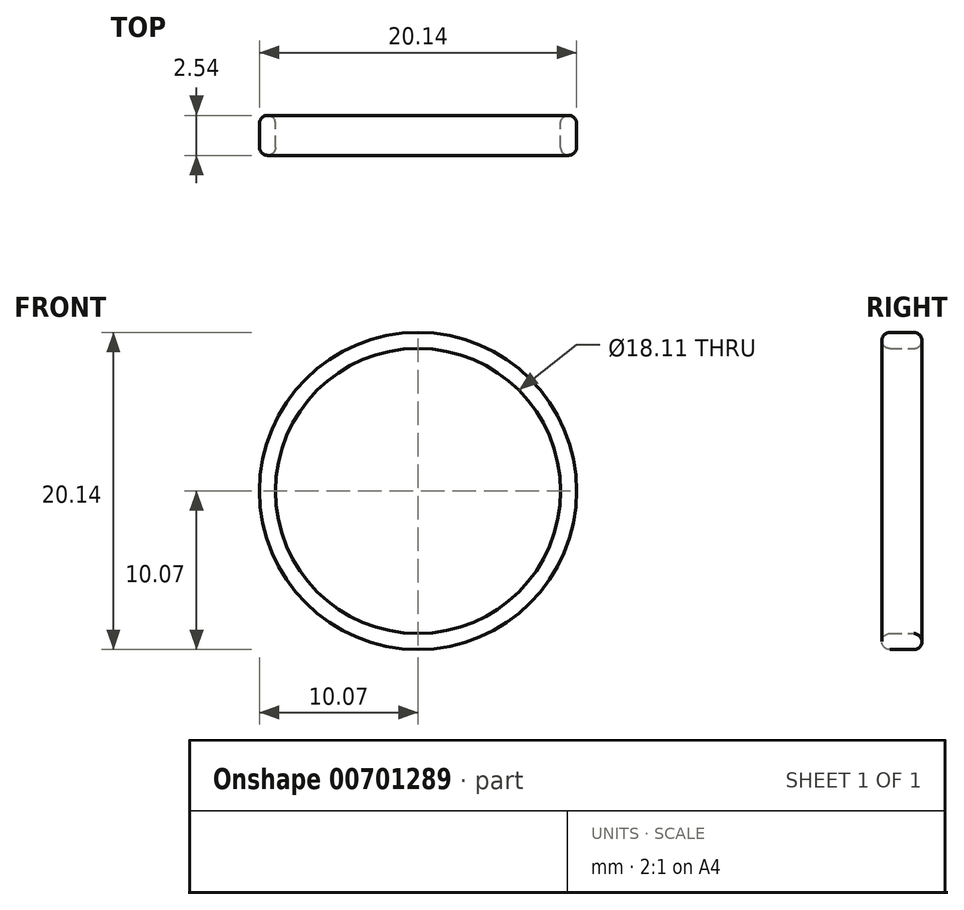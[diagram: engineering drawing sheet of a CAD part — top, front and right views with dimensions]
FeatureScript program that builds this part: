
annotation { "Feature Type Name" : "Feature", "Feature Type Description" : "" }
export const myFeature = defineFeature(function(context is Context, id is Id, definition is map)
    precondition{}
    {
        {
            var Q0;
            Q0=qCreatedBy(makeId("Front.planeOp"),FACE);
            var sketch = newSketch(context, id + "F0", { "sketchPlane" : qUnion([Q0])});
            skCircle(sketch, "E0", {"center": v(0, 0) * mm, "radius": 9.06 * mm});
            skCircle(sketch, "E1", {"center": v(0, 0) * mm, "radius": 10.07 * mm});
            skSolve(sketch);
        }
        {
            var Q0;
            Q0 = qSketchRegion(id + "F0", true);
            extrude(context, id + "F1", {"entities" : qUnion([Q0]), "endBound" : BoundingType.SYMMETRIC, "depth" : 2.54 * mm, "offsetDistance" : 25.4 * mm});
        }
        {
            var Q0;
            Q0=makeQuery(id+"F1.opExtrude","CAP_EDGE",EDGE,{"disambiguationData":[OSD([sQuery(id+"F0.wireOp",EDGE,"E0")])],"isStart":false});
            var Q1;
            Q1=makeQuery(id+"F1.opExtrude","CAP_EDGE",EDGE,{"disambiguationData":[OSD([sQuery(id+"F0.wireOp",EDGE,"E0")])],"isStart":true});
            var Q2;
            Q2=makeQuery(id+"F1.opExtrude","CAP_EDGE",EDGE,{"disambiguationData":[OSD([sQuery(id+"F0.wireOp",EDGE,"E1")])],"isStart":false});
            var Q3;
            Q3=makeQuery(id+"F1.opExtrude","SWEPT_FACE",FACE,{"disambiguationData":[OSD([sQuery(id+"F0.wireOp",EDGE,"E1")])]});
            fillet(context, id + "F2", {"entities" : qUnion([Q0, Q1, Q2, Q3]), "radius" : 0.5 * mm, "tangentPropagation" : true, "allowEdgeOverflow" : false});
        }
    });
